# Revit family: Security-Safe
name_source: partatom
category: Generic Models
units: mm (PartAtom-declared; Revit-internal decimal feet)

## family parameters
Always vertical = Yes
Can host rebar = No
Classification Number = 23.40.70.27
Cut with Voids When Loaded = No
Maintain Annotation Orientation = No
Part Type = Normal
Room Calculation Point = No
Round Connector Dimension = Use Diameter
Shared = No
Work Plane-Based = No

## types (1)
- Security-Safe
    Accent Material = ARCAT - Metal - Brass_Polished
    Assembly Code = E1010120
    Body Material = ARCAT - Metal - Steel - Painted_Grey
    Construction Details = http://www.arcat.com
    Default Elevation = 0' - 0"
    Description = Security Safe
    Drop Slot Width = 0' - 4"
    Expected Lifespan (Years) = 50
    Fire Rating_Hours = 2
    Green Building-LEED = http://www.arcat.com
    Hardware Material = ARCAT - Metal - Steel - Stainless
    Height = 1' - 5"
    Hinge Material = ARCAT - Metal - Steel - Painted_Grey
    Keynote = 11020
    Length = 1' - 8"
    Lock Type = 3 number mechanical combination lock, 1-60 Numbering
    Maintenance Schedule (Months) = 12
    Manufacturer = Generic
    Manufacturer Fax = (203) 939-2444
    Manufacturer Website = http://www.arcat.com
    Material Unit Weight = 200.00 lb/ft³
    Model = Generic
    Product Data = http://www.arcat.com
    Product Properties = http://www.arcat.com
    Specification = http://www.arcat.com
    Storage Volume = 2.04 CF
    Total Volume = 2.36 CF
    Warranty Duration (Years) = 10
    Weight = 64.91 lb
    Width = 1' - 0"
    matlvol = 0.32 CF

## geometry (parser evidence)
native form markers: Sweep x4
no freeform markers — native parametric forms only
